AUTODESK INVENTOR PART (.ipt)
format: ipt  version: 2016 SP2 (Build 200236200, 236)  size: 2,704,384 bytes
history: native  units: mm
features: imported_body x256, other x2, sketch x1
ambient origin geometry x8: Origin, YZ Plane, XZ Plane, XY Plane, X Axis, Y Axis, Z Axis, Center Point
bodies: Solid1 (feature_tree), Solid2 (feature_tree), Solid3 (feature_tree), Solid4 (feature_tree), Solid5 (feature_tree), Solid6 (feature_tree), Solid7 (feature_tree), Solid8 (feature_tree), Solid9 (feature_tree), Solid10 (feature_tree), Solid11 (feature_tree), Solid12 (feature_tree), Solid13 (feature_tree), Solid14 (feature_tree), Solid15 (feature_tree), Solid16 (feature_tree), Solid17 (feature_tree), Solid18 (feature_tree), Solid19 (feature_tree), Solid20 (feature_tree), Solid21 (feature_tree), Solid22 (feature_tree), Solid23 (feature_tree), Solid24 (feature_tree), Solid25 (feature_tree), Solid26 (feature_tree), Solid27 (feature_tree), Solid28 (feature_tree), Solid29 (feature_tree), Solid30 (feature_tree), Solid31 (feature_tree), Solid32 (feature_tree), Solid33 (feature_tree), Solid34 (feature_tree), Solid35 (feature_tree), Solid36 (feature_tree), Solid37 (feature_tree), Solid38 (feature_tree), Solid39 (feature_tree), Solid40 (feature_tree), Solid41 (feature_tree), Solid42 (feature_tree), Solid43 (feature_tree), Solid44 (feature_tree), Solid45 (feature_tree), Solid46 (feature_tree), Solid47 (feature_tree), Solid48 (feature_tree), Solid49 (feature_tree), Solid50 (feature_tree), Solid51 (feature_tree), Solid52 (feature_tree), Solid53 (feature_tree), Solid54 (feature_tree), Solid55 (feature_tree), Solid56 (feature_tree), Solid57 (feature_tree), Solid58 (feature_tree), Solid59 (feature_tree), Solid60 (feature_tree), Solid61 (feature_tree), Solid62 (feature_tree), Solid63 (feature_tree), Solid64 (feature_tree), Solid65 (feature_tree), Solid66 (feature_tree), Solid67 (feature_tree), Solid68 (feature_tree), Solid69 (feature_tree), Solid70 (feature_tree), Solid71 (feature_tree), Solid72 (feature_tree), Solid73 (feature_tree), Solid74 (feature_tree), Solid75 (feature_tree), Solid76 (feature_tree), Solid77 (feature_tree), Solid78 (feature_tree), Solid79 (feature_tree), Solid80 (feature_tree), Solid81 (feature_tree), Solid82 (feature_tree), Solid83 (feature_tree), Solid84 (feature_tree), Solid85 (feature_tree), Solid86 (feature_tree), Solid87 (feature_tree), Solid88 (feature_tree), Solid89 (feature_tree), Solid90 (feature_tree), Solid91 (feature_tree), Solid92 (feature_tree), Solid93 (feature_tree), Solid94 (feature_tree), Solid95 (feature_tree), Solid96 (feature_tree), Solid97 (feature_tree), Solid98 (feature_tree), Solid99 (feature_tree), Solid100 (feature_tree), Solid101 (feature_tree), Solid102 (feature_tree), Solid103 (feature_tree), Solid104 (feature_tree), Solid105 (feature_tree), Solid106 (feature_tree), Solid107 (feature_tree), Solid108 (feature_tree), Solid109 (feature_tree), Solid110 (feature_tree), Solid111 (feature_tree), Solid112 (feature_tree), Solid113 (feature_tree), Solid114 (feature_tree), Solid115 (feature_tree), Solid116 (feature_tree), Solid117 (feature_tree), Solid118 (feature_tree), Solid119 (feature_tree), Solid120 (feature_tree), Solid121 (feature_tree), Solid122 (feature_tree), Solid123 (feature_tree), Solid124 (feature_tree), Solid125 (feature_tree), Solid126 (feature_tree), Solid127 (feature_tree), Solid128 (feature_tree), Solid129 (feature_tree), Solid130 (feature_tree), Solid131 (feature_tree), Solid132 (feature_tree), Solid133 (feature_tree), Solid134 (feature_tree), Solid135 (feature_tree), Solid136 (feature_tree), Solid137 (feature_tree), Solid138 (feature_tree), Solid139 (feature_tree), Solid140 (feature_tree), Solid141 (feature_tree), Solid142 (feature_tree), Solid143 (feature_tree), Solid144 (feature_tree), Solid145 (feature_tree), Solid146 (feature_tree), Solid147 (feature_tree), Solid148 (feature_tree), Solid149 (feature_tree), Solid150 (feature_tree), Solid151 (feature_tree), Solid152 (feature_tree), Solid153 (feature_tree), Solid154 (feature_tree), Solid155 (feature_tree), Solid156 (feature_tree), Solid157 (feature_tree), Solid158 (feature_tree), Solid159 (feature_tree), Solid160 (feature_tree), Solid161 (feature_tree), Solid162 (feature_tree), Solid163 (feature_tree), Solid164 (feature_tree), Solid165 (feature_tree), Solid166 (feature_tree), Solid167 (feature_tree), Solid168 (feature_tree), Solid169 (feature_tree), Solid170 (feature_tree), Solid171 (feature_tree), Solid172 (feature_tree), Solid173 (feature_tree), Solid174 (feature_tree), Solid175 (feature_tree), Solid176 (feature_tree), Solid177 (feature_tree), Solid178 (feature_tree), Solid179 (feature_tree), Solid180 (feature_tree), Solid181 (feature_tree), Solid182 (feature_tree), Solid183 (feature_tree), Solid184 (feature_tree), Solid185 (feature_tree), Solid186 (feature_tree), Solid187 (feature_tree), Solid188 (feature_tree), Solid189 (feature_tree), Solid190 (feature_tree), Solid191 (feature_tree), Solid192 (feature_tree), Solid193 (feature_tree), Solid194 (feature_tree), Solid195 (feature_tree), Solid196 (feature_tree), Solid197 (feature_tree), Solid198 (feature_tree), Solid199 (feature_tree), Solid200 (feature_tree), Solid201 (feature_tree), Solid202 (feature_tree), Solid203 (feature_tree), Solid204 (feature_tree), Solid205 (feature_tree), Solid206 (feature_tree), Solid207 (feature_tree), Solid208 (feature_tree), Solid209 (feature_tree), Solid210 (feature_tree), Solid211 (feature_tree), Solid212 (feature_tree), Solid213 (feature_tree), Solid214 (feature_tree), Solid215 (feature_tree), Solid216 (feature_tree), Solid217 (feature_tree), Solid218 (feature_tree), Solid219 (feature_tree), Solid220 (feature_tree), Solid221 (feature_tree), Solid222 (feature_tree), Solid223 (feature_tree), Solid224 (feature_tree), Solid225 (feature_tree), Solid226 (feature_tree), Solid227 (feature_tree), Solid228 (feature_tree), Solid229 (feature_tree), Solid230 (feature_tree), Solid231 (feature_tree), Solid232 (feature_tree), Solid233 (feature_tree), Solid234 (feature_tree), Solid235 (feature_tree), Solid236 (feature_tree), Solid237 (feature_tree), Solid238 (feature_tree), Solid239 (feature_tree), Solid240 (feature_tree), Solid241 (feature_tree), Solid242 (feature_tree), Solid243 (feature_tree), Solid244 (feature_tree), Solid245 (feature_tree), Solid246 (feature_tree), Solid247 (feature_tree), Solid248 (feature_tree), Solid249 (feature_tree), Solid250 (feature_tree), Solid251 (feature_tree), Solid252 (feature_tree), Solid253 (feature_tree), Solid254 (feature_tree), Solid255 (feature_tree), Solid256 (feature_tree)
feature tree (259):
  sketch  "Sketch1"
  imported_body  "Base1"
  imported_body  "Base2"
  imported_body  "Base3"
  imported_body  "Base4"
  imported_body  "Base5"
  imported_body  "Base6"
  imported_body  "Base7"
  imported_body  "Base8"
  imported_body  "Base9"
  imported_body  "Base10"
  imported_body  "Base11"
  imported_body  "Base12"
  imported_body  "Base13"
  imported_body  "Base14"
  imported_body  "Base15"
  imported_body  "Base16"
  imported_body  "Base17"
  imported_body  "Base18"
  imported_body  "Base19"
  imported_body  "Base20"
  imported_body  "Base21"
  imported_body  "Base22"
  imported_body  "Base23"
  imported_body  "Base24"
  imported_body  "Base25"
  imported_body  "Base26"
  imported_body  "Base27"
  imported_body  "Base28"
  imported_body  "Base29"
  imported_body  "Base30"
  imported_body  "Base31"
  imported_body  "Base32"
  imported_body  "Base33"
  imported_body  "Base34"
  imported_body  "Base35"
  imported_body  "Base36"
  imported_body  "Base37"
  imported_body  "Base38"
  imported_body  "Base39"
  imported_body  "Base40"
  imported_body  "Base41"
  imported_body  "Base42"
  imported_body  "Base43"
  imported_body  "Base44"
  imported_body  "Base45"
  imported_body  "Base46"
  imported_body  "Base47"
  imported_body  "Base48"
  imported_body  "Base49"
  imported_body  "Base50"
  imported_body  "Base51"
  imported_body  "Base52"
  imported_body  "Base53"
  imported_body  "Base54"
  imported_body  "Base55"
  imported_body  "Base56"
  imported_body  "Base57"
  imported_body  "Base58"
  imported_body  "Base59"
  imported_body  "Base60"
  imported_body  "Base61"
  imported_body  "Base62"
  imported_body  "Base63"
  imported_body  "Base64"
  imported_body  "Base65"
  imported_body  "Base66"
  imported_body  "Base67"
  imported_body  "Base68"
  imported_body  "Base69"
  imported_body  "Base70"
  imported_body  "Base71"
  imported_body  "Base72"
  imported_body  "Base73"
  imported_body  "Base74"
  imported_body  "Base75"
  imported_body  "Base76"
  imported_body  "Base77"
  imported_body  "Base78"
  imported_body  "Base79"
  imported_body  "Base80"
  imported_body  "Base81"
  imported_body  "Base82"
  imported_body  "Base83"
  imported_body  "Base84"
  imported_body  "Base85"
  imported_body  "Base86"
  imported_body  "Base87"
  imported_body  "Base88"
  imported_body  "Base89"
  imported_body  "Base90"
  imported_body  "Base91"
  imported_body  "Base92"
  imported_body  "Base93"
  imported_body  "Base94"
  imported_body  "Base95"
  imported_body  "Base96"
  imported_body  "Base97"
  imported_body  "Base98"
  imported_body  "Base99"
  imported_body  "Base100"
  imported_body  "Base101"
  imported_body  "Base102"
  imported_body  "Base103"
  imported_body  "Base104"
  imported_body  "Base105"
  imported_body  "Base106"
  imported_body  "Base107"
  imported_body  "Base108"
  imported_body  "Base109"
  imported_body  "Base110"
  imported_body  "Base111"
  imported_body  "Base112"
  imported_body  "Base113"
  imported_body  "Base114"
  imported_body  "Base115"
  imported_body  "Base116"
  imported_body  "Base117"
  imported_body  "Base118"
  imported_body  "Base119"
  imported_body  "Base120"
  imported_body  "Base121"
  imported_body  "Base122"
  imported_body  "Base123"
  imported_body  "Base124"
  imported_body  "Base125"
  imported_body  "Base126"
  imported_body  "Base127"
  imported_body  "Base128"
  imported_body  "Base129"
  imported_body  "Base130"
  imported_body  "Base131"
  imported_body  "Base132"
  imported_body  "Base133"
  imported_body  "Base134"
  imported_body  "Base135"
  imported_body  "Base136"
  imported_body  "Base137"
  imported_body  "Base138"
  imported_body  "Base139"
  imported_body  "Base140"
  imported_body  "Base141"
  imported_body  "Base142"
  imported_body  "Base143"
  imported_body  "Base144"
  imported_body  "Base145"
  imported_body  "Base146"
  imported_body  "Base147"
  imported_body  "Base148"
  imported_body  "Base149"
  imported_body  "Base150"
  imported_body  "Base151"
  imported_body  "Base152"
  imported_body  "Base153"
  imported_body  "Base154"
  imported_body  "Base155"
  imported_body  "Base156"
  imported_body  "Base157"
  imported_body  "Base158"
  imported_body  "Base159"
  imported_body  "Base160"
  imported_body  "Base161"
  imported_body  "Base162"
  imported_body  "Base163"
  imported_body  "Base164"
  imported_body  "Base165"
  imported_body  "Base166"
  imported_body  "Base167"
  imported_body  "Base168"
  imported_body  "Base169"
  imported_body  "Base170"
  imported_body  "Base171"
  imported_body  "Base172"
  imported_body  "Base173"
  imported_body  "Base174"
  imported_body  "Base175"
  imported_body  "Base176"
  imported_body  "Base177"
  imported_body  "Base178"
  imported_body  "Base179"
  imported_body  "Base180"
  imported_body  "Base181"
  imported_body  "Base182"
  imported_body  "Base183"
  imported_body  "Base184"
  imported_body  "Base185"
  imported_body  "Base186"
  imported_body  "Base187"
  imported_body  "Base188"
  imported_body  "Base189"
  imported_body  "Base190"
  imported_body  "Base191"
  imported_body  "Base192"
  imported_body  "Base193"
  imported_body  "Base194"
  imported_body  "Base195"
  imported_body  "Base196"
  imported_body  "Base197"
  imported_body  "Base198"
  imported_body  "Base199"
  imported_body  "Base200"
  imported_body  "Base201"
  imported_body  "Base202"
  imported_body  "Base203"
  imported_body  "Base204"
  imported_body  "Base205"
  imported_body  "Base206"
  imported_body  "Base207"
  imported_body  "Base208"
  imported_body  "Base209"
  imported_body  "Base210"
  imported_body  "Base211"
  imported_body  "Base212"
  imported_body  "Base213"
  imported_body  "Base214"
  imported_body  "Base215"
  imported_body  "Base216"
  imported_body  "Base217"
  imported_body  "Base218"
  imported_body  "Base219"
  imported_body  "Base220"
  imported_body  "Base221"
  imported_body  "Base222"
  imported_body  "Base223"
  imported_body  "Base224"
  imported_body  "Base225"
  imported_body  "Base226"
  imported_body  "Base227"
  imported_body  "Base228"
  imported_body  "Base229"
  imported_body  "Base230"
  imported_body  "Base231"
  imported_body  "Base232"
  imported_body  "Base233"
  imported_body  "Base234"
  imported_body  "Base235"
  imported_body  "Base236"
  imported_body  "Base237"
  imported_body  "Base238"
  imported_body  "Base239"
  imported_body  "Base240"
  imported_body  "Base241"
  imported_body  "Base242"
  imported_body  "Base243"
  imported_body  "Base244"
  imported_body  "Base245"
  imported_body  "Base246"
  imported_body  "Base247"
  imported_body  "Base248"
  imported_body  "Base249"
  imported_body  "Base250"
  imported_body  "Base251"
  imported_body  "Base252"
  imported_body  "Base253"
  imported_body  "Base254"
  imported_body  "Base255"
  imported_body  "Base256"
  other  "Composite1"
  other  "Srf1"
